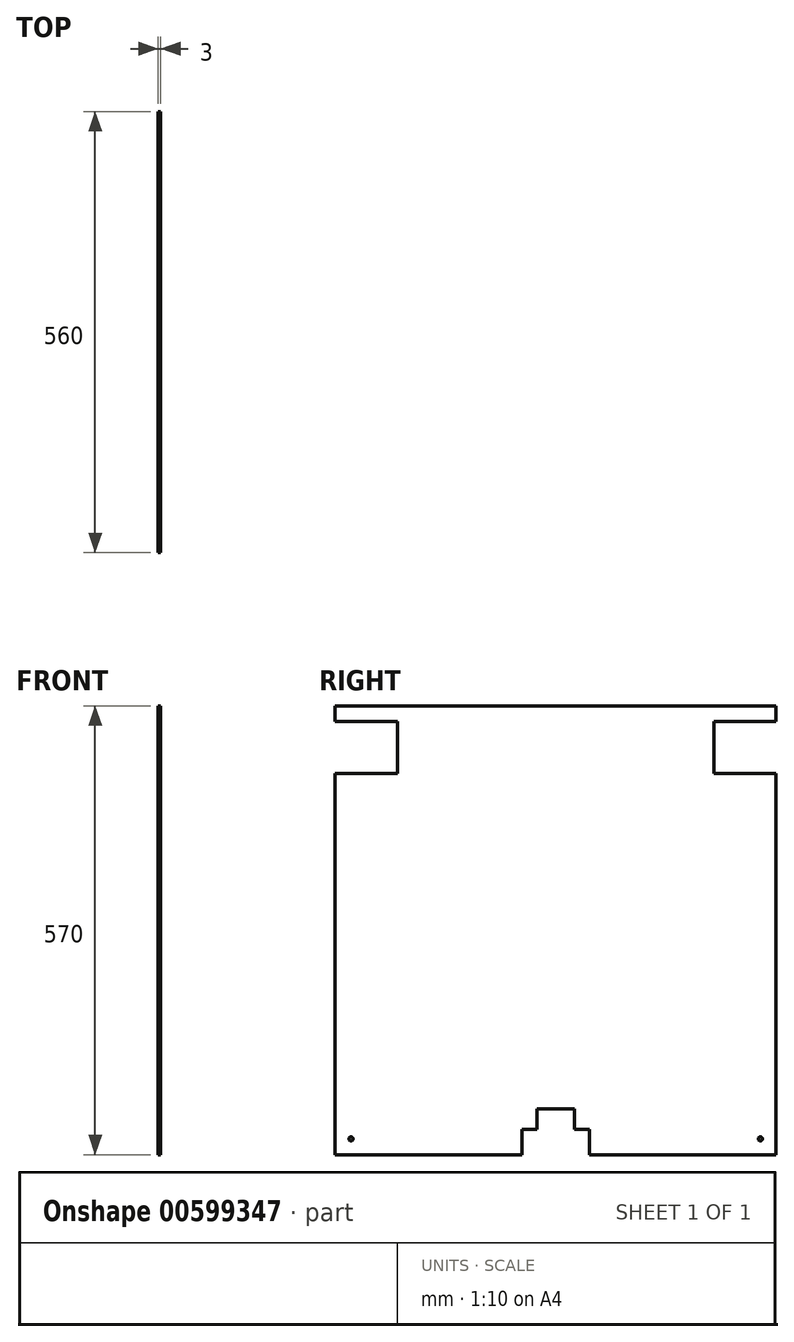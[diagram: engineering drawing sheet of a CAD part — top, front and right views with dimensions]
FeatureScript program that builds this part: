
annotation { "Feature Type Name" : "Feature", "Feature Type Description" : "" }
export const myFeature = defineFeature(function(context is Context, id is Id, definition is map)
    precondition{}
    {
        {
            var Q0;
            Q0=qCreatedBy(makeId("Right.planeOp"),FACE);
            var sketch = newSketch(context, id + "F0", { "sketchPlane" : qUnion([Q0])});
            skLineSegment(sketch, "E0.top", {"start": v(-270, -260) * mm, "end": v(270, -260) * mm, "construction": true});
            skLineSegment(sketch, "E0.left", {"start": v(-270, 214) * mm, "end": v(-270, -260) * mm, "construction": true});
            skLineSegment(sketch, "E0.right", {"start": v(270, 214) * mm, "end": v(270, -260) * mm, "construction": true});
            skCircle(sketch, "E1", {"center": v(-260, -250) * mm, "radius": 2.65 * mm});
            skCircle(sketch, "E2", {"center": v(260, -250) * mm, "radius": 2.65 * mm});
            skLineSegment(sketch, "E3.bottom", {"start": v(270, -260) * mm, "end": v(280, -260) * mm, "construction": true});
            skLineSegment(sketch, "E3.right", {"start": v(280, -260) * mm, "end": v(280, 214) * mm});
            skLineSegment(sketch, "E4.bottom", {"start": v(-270, -260) * mm, "end": v(-280, -260) * mm, "construction": true});
            skLineSegment(sketch, "E4.right", {"start": v(-280, -270) * mm, "end": v(-280, 214) * mm});
            skLineSegment(sketch, "E5.right", {"start": v(-201.22, 300) * mm, "end": v(-201.22, 214) * mm});
            skLineSegment(sketch, "E6.trimOffspring", {"start": v(-201.22, 260) * mm, "end": v(201.22, 260) * mm, "construction": true});
            skLineSegment(sketch, "E7.trimOffspring", {"start": v(-201.22, 300) * mm, "end": v(201.22, 300) * mm});
            skLineSegment(sketch, "E8.MirrorCS", {"start": v(201.22, 300) * mm, "end": v(201.22, 214) * mm});
            skPoint(sketch, "E9.orphan", {"position": v(201.22, 214) * mm});
            skLineSegment(sketch, "E10", {"start": v(-280, -270) * mm, "end": v(-43, -270) * mm});
            skLineSegment(sketch, "E11", {"start": v(280, -270) * mm, "end": v(280, -260) * mm});
            skLineSegment(sketch, "E12", {"start": v(-201.22, 214) * mm, "end": v(-280, 214) * mm});
            skLineSegment(sketch, "E13", {"start": v(280, 214) * mm, "end": v(201.22, 214) * mm});
            skLineSegment(sketch, "E14.top", {"start": v(-24, -212) * mm, "end": v(24, -212) * mm});
            skLineSegment(sketch, "E14.right", {"start": v(24, -238) * mm, "end": v(24, -212) * mm});
            skLineSegment(sketch, "E15.trimOffspring", {"start": v(43, -270) * mm, "end": v(280, -270) * mm});
            skLineSegment(sketch, "E16.bottom", {"start": v(-43, -238) * mm, "end": v(-24, -238) * mm});
            skLineSegment(sketch, "E16.left", {"start": v(-43, -238) * mm, "end": v(-43, -270) * mm});
            skLineSegment(sketch, "E16.right", {"start": v(43, -238) * mm, "end": v(43, -270) * mm});
            skLineSegment(sketch, "E17.trimOffspring", {"start": v(-24, -238) * mm, "end": v(-24, -212) * mm});
            skLineSegment(sketch, "E18.trimOffspring", {"start": v(24, -238) * mm, "end": v(43, -238) * mm});
            skLineSegment(sketch, "E19.bottom", {"start": v(-201.22, 300) * mm, "end": v(-280, 300) * mm});
            skLineSegment(sketch, "E19.top", {"start": v(-201.22, 280) * mm, "end": v(-280, 280) * mm});
            skLineSegment(sketch, "E19.left", {"start": v(-201.22, 300) * mm, "end": v(-201.22, 280) * mm});
            skLineSegment(sketch, "E19.right", {"start": v(-280, 300) * mm, "end": v(-280, 280) * mm});
            skLineSegment(sketch, "E20.bottom", {"start": v(201.22, 300) * mm, "end": v(280, 300) * mm});
            skLineSegment(sketch, "E20.top", {"start": v(201.22, 280) * mm, "end": v(280, 280) * mm});
            skLineSegment(sketch, "E20.left", {"start": v(201.22, 300) * mm, "end": v(201.22, 280) * mm});
            skLineSegment(sketch, "E20.right", {"start": v(280, 300) * mm, "end": v(280, 280) * mm});
            skSolve(sketch);
        }
        {
            var Q0;
            Q0=qSketchRegion(id+"F0",true);
            extrude(context, id + "F1", {"entities" : qUnion([Q0]), "depth" : 3 * mm});
        }
    });
